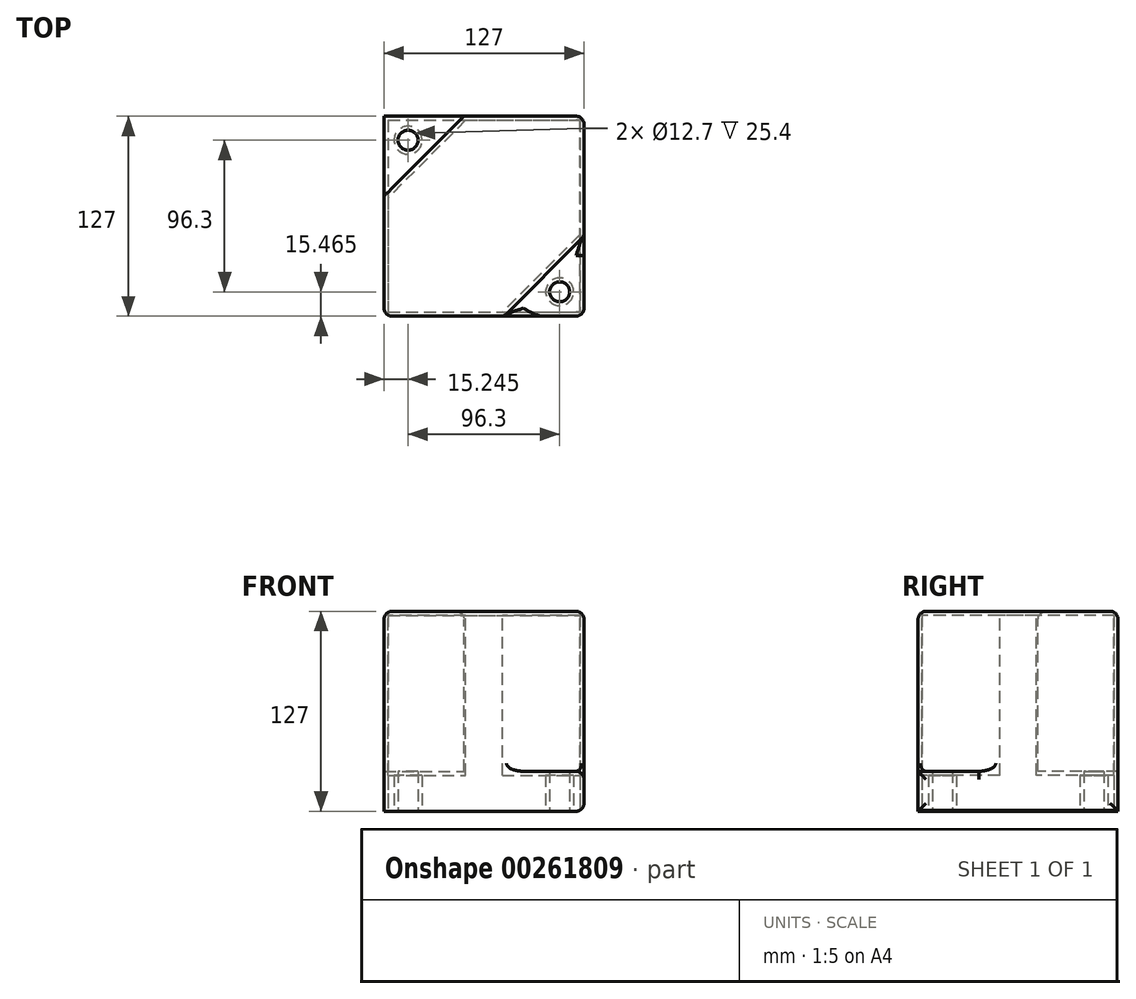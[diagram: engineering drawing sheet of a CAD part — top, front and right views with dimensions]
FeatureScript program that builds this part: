
annotation { "Feature Type Name" : "Feature", "Feature Type Description" : "" }
export const myFeature = defineFeature(function(context is Context, id is Id, definition is map)
    precondition{}
    {
        {
            var Q0;
            Q0=qCreatedBy(makeId("Top.planeOp"),FACE);
            var sketch = newSketch(context, id + "F0", { "sketchPlane" : qUnion([Q0])});
            skLineSegment(sketch, "E0.bottom", {"start": v(-61.59, 71.34) * mm, "end": v(65.41, 71.34) * mm});
            skLineSegment(sketch, "E0.top", {"start": v(-61.59, -55.66) * mm, "end": v(65.41, -55.66) * mm});
            skLineSegment(sketch, "E0.left", {"start": v(-61.59, 71.34) * mm, "end": v(-61.59, -55.66) * mm});
            skLineSegment(sketch, "E0.right", {"start": v(65.41, 71.34) * mm, "end": v(65.41, -55.66) * mm});
            skSolve(sketch);
        }
        {
            var Q0;
            Q0 = qSketchRegion(id + "F0", true);
            extrude(context, id + "F1", {"entities" : qUnion([Q0]), "depth" : 127 * mm});
        }
        {
            var Q0;
            Q0=makeQuery(id+"F1.opExtrude","CAP_FACE",FACE,{"disambiguationData":[OSD([sQuery(id+"F0.wireOp",EDGE,"E0.bottom"),sQuery(id+"F0.wireOp",EDGE,"E0.top"),sQuery(id+"F0.wireOp",EDGE,"E0.left"),sQuery(id+"F0.wireOp",EDGE,"E0.right")])],"isStart":false});
            var sketch = newSketch(context, id + "F2", { "sketchPlane" : qUnion([Q0])});
            skLineSegment(sketch, "E1", {"start": v(65.41, 71.34) * mm, "end": v(-61.59, -55.66) * mm, "construction": true});
            skLineSegment(sketch, "E2", {"start": v(-61.59, 71.34) * mm, "end": v(-10.79, 71.34) * mm});
            skLineSegment(sketch, "E3", {"start": v(-10.79, 71.34) * mm, "end": v(-61.59, 20.54) * mm});
            skLineSegment(sketch, "E4", {"start": v(-61.59, 20.54) * mm, "end": v(-61.59, 71.34) * mm});
            skLineSegment(sketch, "E5.MirrorCS", {"start": v(65.41, -4.86) * mm, "end": v(14.61, -55.66) * mm});
            skLineSegment(sketch, "E6.MirrorCS", {"start": v(65.41, -55.66) * mm, "end": v(65.41, -4.86) * mm});
            skLineSegment(sketch, "E7.MirrorCS", {"start": v(14.61, -55.66) * mm, "end": v(65.41, -55.66) * mm});
            skSolve(sketch);
        }
        {
            var Q0;
            Q0=makeQuery(id+"F2.imprint","IMPRINT",FACE,{"disambiguationData":[TD([[makeQuery(id+"F2.imprint","IMPRINT",EDGE,{"derivedFrom":sQuery(id+"F2.wireOp",EDGE,"E5.MirrorCS")}),1.0]])]});
            var Q1;
            Q1=makeQuery(id+"F2.imprint","IMPRINT",FACE,{"disambiguationData":[TD([[makeQuery(id+"F2.imprint","IMPRINT",EDGE,{"derivedFrom":sQuery(id+"F2.wireOp",EDGE,"E2")}),-1.0]])]});
            extrude(context, id + "F3", {"entities" : qUnion([Q0, Q1]), "operationType" : NewBodyOperationType.REMOVE, "oppositeDirection" : true, "depth" : 101.6 * mm});
        }
        {
            var Q0;
            Q0=qCreatedBy(makeId("Top.planeOp"),FACE);
            var sketch = newSketch(context, id + "F4", { "sketchPlane" : qUnion([Q0])});
            skCircle(sketch, "E8", {"center": v(-46.35, 56.1) * mm, "radius": 6.35 * mm});
            skLineSegment(sketch, "E9", {"start": v(-61.8, -55.65) * mm, "end": v(65.8, 71.96) * mm, "construction": true});
            skCircle(sketch, "E10.MirrorC", {"center": v(49.96, -40.2) * mm, "radius": 6.35 * mm});
            skSolve(sketch);
        }
        {
            var Q0;
            Q0 = qSketchRegion(id + "F4", true);
            extrude(context, id + "F5", {"entities" : qUnion([Q0]), "operationType" : NewBodyOperationType.REMOVE, "depth" : 203.2 * mm});
        }
        {
            var Q0;
            Q0=makeQuery(id+"F1.opExtrude","CAP_FACE",FACE,{"disambiguationData":[OSD([sQuery(id+"F0.wireOp",EDGE,"E0.bottom"),sQuery(id+"F0.wireOp",EDGE,"E0.top"),sQuery(id+"F0.wireOp",EDGE,"E0.left"),sQuery(id+"F0.wireOp",EDGE,"E0.right")])],"isStart":true});
            shell(context, id + "F6", {"entities" : qUnion([Q0]), "thickness" : 2.54 * mm});
        }
        {
            var Q0;
            Q0=makeQuery(id+"F1.opExtrude","CAP_EDGE",EDGE,{"disambiguationData":[OSD([sQuery(id+"F0.wireOp",EDGE,"E0.left")])],"isStart":false});
            var Q1;
            Q1=makeQuery(id+"F1.opExtrude","CAP_EDGE",EDGE,{"disambiguationData":[OSD([sQuery(id+"F0.wireOp",EDGE,"E0.top")])],"isStart":false});
            var Q2;
            Q2=makeQuery(id+"F3.boolean.opBoolean","COPY",EDGE,{"derivedFrom":makeQuery(id+"F3.opExtrude","CAP_EDGE",EDGE,{"disambiguationData":[OSD([sQuery(id+"F2.wireOp",EDGE,"E5.MirrorCS")])],"isStart":true})});
            var Q3;
            Q3=makeQuery(id+"F1.opExtrude","CAP_EDGE",EDGE,{"disambiguationData":[OSD([sQuery(id+"F0.wireOp",EDGE,"E0.right")])],"isStart":false});
            var Q4;
            Q4=makeQuery(id+"F1.opExtrude","CAP_EDGE",EDGE,{"disambiguationData":[OSD([sQuery(id+"F0.wireOp",EDGE,"E0.bottom")])],"isStart":false});
            var Q5;
            Q5=makeQuery(id+"F3.boolean.opBoolean","COPY",EDGE,{"derivedFrom":makeQuery(id+"F3.opExtrude","CAP_EDGE",EDGE,{"disambiguationData":[OSD([sQuery(id+"F2.wireOp",EDGE,"E3")])],"isStart":true})});
            var Q6;
            Q6=makeQuery(id+"F3.boolean.opBoolean","COPY",FACE,{"derivedFrom":makeQuery(id+"F3.opExtrude","SWEPT_FACE",FACE,{"disambiguationData":[OSD([sQuery(id+"F2.wireOp",EDGE,"E5.MirrorCS")])]})});
            var Q7;
            Q7=makeQuery(id+"F1.opExtrude","SWEPT_EDGE",EDGE,{"disambiguationData":[OSD([sQuery(id+"F0.wireOp",EDGE,"E0.top"),sQuery(id+"F0.wireOp",EDGE,"E0.left")])]});
            var Q8;
            Q8=makeQuery(id+"F1.opExtrude","CAP_EDGE",EDGE,{"disambiguationData":[OSD([sQuery(id+"F0.wireOp",EDGE,"E0.right")])],"isStart":true});
            var Q9;
            Q9=makeQuery(id+"F1.opExtrude","SWEPT_FACE",FACE,{"disambiguationData":[OSD([sQuery(id+"F0.wireOp",EDGE,"E0.right")])]});
            var Q10;
            Q10=makeQuery(id+"F3.boolean.opBoolean","COPY",EDGE,{"derivedFrom":makeQuery(id+"F3.opExtrude","CAP_EDGE",EDGE,{"disambiguationData":[OSD([sQuery(id+"F2.wireOp",EDGE,"E7.MirrorCS")])],"isStart":false})});
            fillet(context, id + "F7", {"entities" : qUnion([Q0, Q1, Q2, Q3, Q4, Q5, Q6, Q7, Q8, Q9, Q10]), "radius" : 5.08 * mm, "tangentPropagation" : true, "allowEdgeOverflow" : false});
        }
    });
